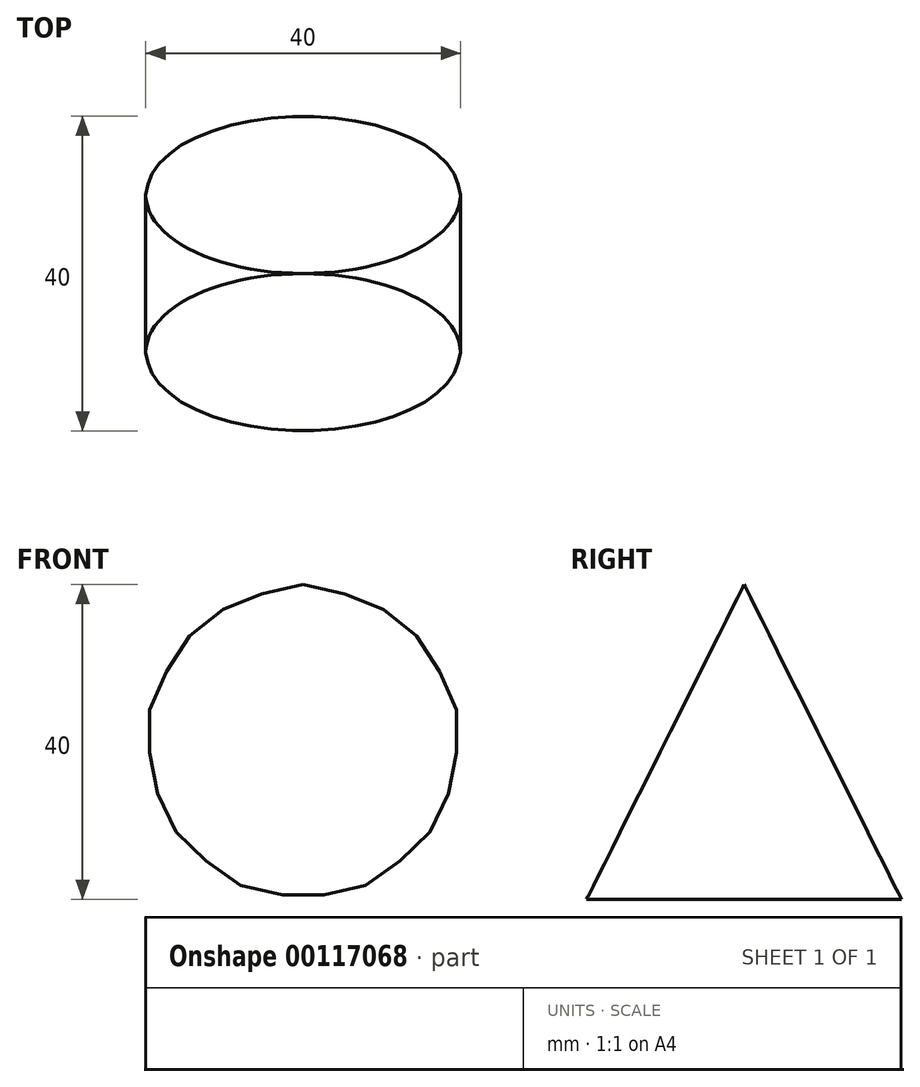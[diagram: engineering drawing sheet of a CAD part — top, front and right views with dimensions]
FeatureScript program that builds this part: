
annotation { "Feature Type Name" : "Feature", "Feature Type Description" : "" }
export const myFeature = defineFeature(function(context is Context, id is Id, definition is map)
    precondition{}
    {
        {
            var Q0;
            Q0=qCreatedBy(makeId("Front.planeOp"),FACE);
            var sketch = newSketch(context, id + "F0", { "sketchPlane" : qUnion([Q0])});
            skCircle(sketch, "E0", {"center": v(0, 0) * mm, "radius": 20 * mm});
            skSolve(sketch);
        }
        {
            var Q0;
            Q0 = qSketchRegion(id + "F0", true);
            extrude(context, id + "F1", {"entities" : qUnion([Q0]), "depth" : 40 * mm});
        }
        {
            var Q0;
            Q0=qCreatedBy(makeId("Right.planeOp"),FACE);
            var sketch = newSketch(context, id + "F2", { "sketchPlane" : qUnion([Q0])});
            skLineSegment(sketch, "E1", {"start": v(-20, 20) * mm, "end": v(-40, -20) * mm});
            skLineSegment(sketch, "E2", {"start": v(-40, -20) * mm, "end": v(0, -20) * mm});
            skLineSegment(sketch, "E3", {"start": v(0, -20) * mm, "end": v(-20, 20) * mm});
            skLineSegment(sketch, "E4.bottom", {"start": v(-63.82, 37.15) * mm, "end": v(35.48, 37.15) * mm});
            skLineSegment(sketch, "E4.top", {"start": v(-63.82, -35.96) * mm, "end": v(35.48, -35.96) * mm});
            skLineSegment(sketch, "E4.left", {"start": v(-63.82, 37.15) * mm, "end": v(-63.82, -35.96) * mm});
            skLineSegment(sketch, "E4.right", {"start": v(35.48, 37.15) * mm, "end": v(35.48, -35.96) * mm});
            skSolve(sketch);
        }
        {
            var Q0;
            Q0 = qSketchRegion(id + "F2", true);
            extrude(context, id + "F3", {"entities" : qUnion([Q0]), "operationType" : NewBodyOperationType.REMOVE, "endBound" : BoundingType.THROUGH_ALL, "oppositeDirection" : true, "depth" : 25.4 * mm, "hasSecondDirection" : true, "secondDirectionBound" : SecondDirectionBoundingType.THROUGH_ALL, "secondDirectionOppositeDirection" : false, "secondDirectionDepth" : 25.4 * mm});
        }
    });
